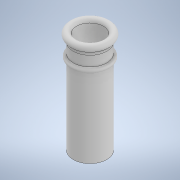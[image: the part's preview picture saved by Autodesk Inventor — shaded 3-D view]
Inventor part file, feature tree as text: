
AUTODESK INVENTOR PART (.ipt)
format: ipt  version: 2021 (Build 250183000, 183)  size: 169,984 bytes
history: native  units: mm
features: sketch x5, extrude x4, projected_geometry x3, revolve x1
ambient origin geometry x8: Origin, YZ Plane, XZ Plane, XY Plane, X Axis, Y Axis, Z Axis, Center Point
bodies: Volumenkörper1 (feature_tree)
feature tree (13):
  extrude  "Extrusion1"  Depth=25.0mm TaperAngle=0.0deg
  extrude  "Extrusion2"  Depth=5.0mm
  extrude  "Extrusion3"  Depth=1.0mm
  revolve  "Umdrehung1"
  extrude  "Extrusion4"  Depth=5.0mm
  sketch  "Skizze1"  dims[d0=10.0mm d1=25.0mm d2=0.0mm]
  sketch  "Skizze2"  dims[d3=7.0mm d4=5.0mm]
  projected_geometry  "Projizierte Kontur1"
  sketch  "Skizze3"  dims[d5=10.0mm d6=0.0mm d7=1.0mm]
  sketch  "Skizze4"  dims[d8=5.0mm d9=0.0mm d10=5.0mm]
  projected_geometry  "Projizierte Kontur2"
  sketch  "Skizze5"  dims[d11=0.75mm d12=2.0mm d13=1.0mm d14=1.0mm d15=90.0deg d16=20.0mm d17=0.0mm]
  projected_geometry  "Projizierte Kontur3"
